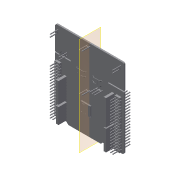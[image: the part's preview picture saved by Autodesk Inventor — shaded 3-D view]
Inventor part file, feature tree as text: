
AUTODESK INVENTOR PART (.ipt)
format: ipt  version: 2016 (Build 200138000, 138)  size: 3,458,560 bytes
history: native  units: in
note: dims shown in document units (in); Inventor stores cm internally (conversion verified against a paired STEP export)
features: other x3, plane x1
ambient origin geometry x8: Origin, YZ Plane, XZ Plane, XY Plane, X Axis, Y Axis, Z Axis, Center Point
bodies: Body1 (feature_tree), Body2 (feature_tree), Body3 (feature_tree), Body4 (feature_tree), Body5 (feature_tree), Body6 (feature_tree), Body7 (feature_tree), Body8 (feature_tree), Body9 (feature_tree), Body10 (feature_tree), Body11 (feature_tree), Body12 (feature_tree), Body13 (feature_tree), Body14 (feature_tree), Body15 (feature_tree), Body16 (feature_tree), Body17 (feature_tree), Body18 (feature_tree), Body19 (feature_tree), Body20 (feature_tree), Body21 (feature_tree)
feature tree (4):
  other  "nucleo_boardNUCLEO-F411RE.iam"
  other  "nucleo_boardNUCLEO-F411RE.iam_Bodies"
  plane  "Work Plane1"
  other  "Srf1"
